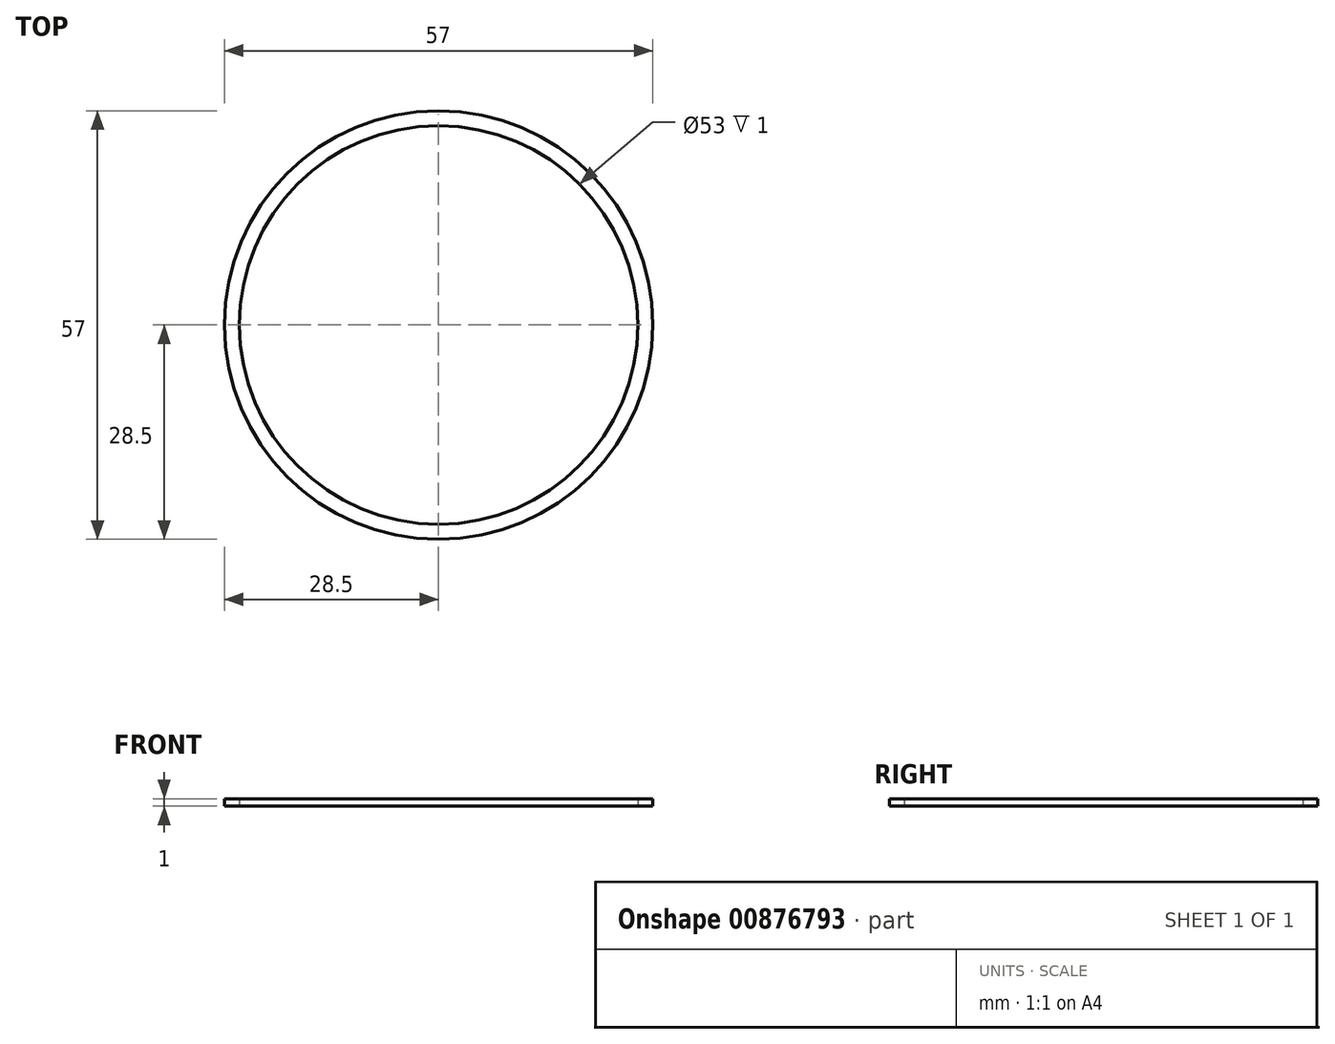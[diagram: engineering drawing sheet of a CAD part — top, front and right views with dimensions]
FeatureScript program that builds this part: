
annotation { "Feature Type Name" : "Feature", "Feature Type Description" : "" }
export const myFeature = defineFeature(function(context is Context, id is Id, definition is map)
    precondition{}
    {
        {
            var Q0;
            Q0=qCreatedBy(makeId("Top.planeOp"),FACE);
            var sketch = newSketch(context, id + "F0", { "sketchPlane" : qUnion([Q0])});
            skCircle(sketch, "E0", {"center": v(0, 0) * mm, "radius": 28.5 * mm});
            skCircle(sketch, "E1", {"center": v(0, 0) * mm, "radius": 26.5 * mm});
            skCircle(sketch, "E2", {"center": v(0, 0) * mm, "radius": 25 * mm, "construction": true});
            skLineSegment(sketch, "E3", {"start": v(0, 0) * mm, "end": v(0, -38.84) * mm, "construction": true});
            skLineSegment(sketch, "E4", {"start": v(0, 0) * mm, "end": v(0, 38.39) * mm, "construction": true});
            skPoint(sketch, "E5", {"position": v(0, -26.5) * mm});
            skPoint(sketch, "E6", {"position": v(0, 26.5) * mm});
            skLineSegment(sketch, "E7.bottom", {"start": v(0, 26.5) * mm, "end": v(2, 26.5) * mm, "construction": true});
            skLineSegment(sketch, "E7.top", {"start": v(0, -26.5) * mm, "end": v(2, -26.5) * mm, "construction": true});
            skLineSegment(sketch, "E7.left", {"start": v(0, 26.5) * mm, "end": v(0, -26.5) * mm, "construction": true});
            skLineSegment(sketch, "E7.right", {"start": v(2, 26.5) * mm, "end": v(2, -26.5) * mm, "construction": true});
            skLineSegment(sketch, "E8", {"start": v(0, 0) * mm, "end": v(3.9, -37.2) * mm, "construction": true});
            skLineSegment(sketch, "E9", {"start": v(0, 0) * mm, "end": v(-3.88, -36.95) * mm, "construction": true});
            skLineSegment(sketch, "E10", {"start": v(0, 0) * mm, "end": v(3.82, 36.34) * mm, "construction": true});
            skLineSegment(sketch, "E11", {"start": v(0, 0) * mm, "end": v(-3.79, 36.02) * mm, "construction": true});
            skLineSegment(sketch, "E12", {"start": v(0, 0) * mm, "end": v(12, 0) * mm, "construction": true});
            skCircle(sketch, "E13", {"center": v(12, 0) * mm, "radius": 9 * mm, "construction": true});
            skLineSegment(sketch, "E14", {"start": v(0, 0) * mm, "end": v(38.58, -9.62) * mm, "construction": true});
            skLineSegment(sketch, "E15", {"start": v(0, 0) * mm, "end": v(37.47, 9.34) * mm, "construction": true});
            skLineSegment(sketch, "E16", {"start": v(0, 0) * mm, "end": v(-36.64, 9.13) * mm, "construction": true});
            skLineSegment(sketch, "E17", {"start": v(0, 0) * mm, "end": v(-36.6, -9.13) * mm, "construction": true});
            skLineSegment(sketch, "E18", {"start": v(0, 0) * mm, "end": v(8.88, 35.6) * mm, "construction": true});
            skLineSegment(sketch, "E19", {"start": v(0, 0) * mm, "end": v(14.73, 33.1) * mm, "construction": true});
            skLineSegment(sketch, "E20", {"start": v(0, 0) * mm, "end": v(-8.58, 34.42) * mm, "construction": true});
            skLineSegment(sketch, "E21", {"start": v(0, 0) * mm, "end": v(-14.75, 33.13) * mm, "construction": true});
            skLineSegment(sketch, "E22", {"start": v(0, 0) * mm, "end": v(17.52, -30.35) * mm, "construction": true});
            skLineSegment(sketch, "E23", {"start": v(0, 0) * mm, "end": v(22.58, -26.91) * mm, "construction": true});
            skLineSegment(sketch, "E24", {"start": v(0, 0) * mm, "end": v(-16.88, -29.24) * mm, "construction": true});
            skLineSegment(sketch, "E25", {"start": v(0, 0) * mm, "end": v(-21.68, -25.84) * mm, "construction": true});
            skSolve(sketch);
        }
        {
            var Q0;
            Q0=makeQuery(id+"F0.imprint","IMPRINT",FACE,{"disambiguationData":[TD([[makeQuery(id+"F0.imprint","IMPRINT",EDGE,{"derivedFrom":sQuery(id+"F0.wireOp",EDGE,"E0")}),1.0]])]});
            extrude(context, id + "F1", {"entities" : qUnion([Q0]), "depth" : 1 * mm, "offsetDistance" : 25 * mm});
        }
    });
